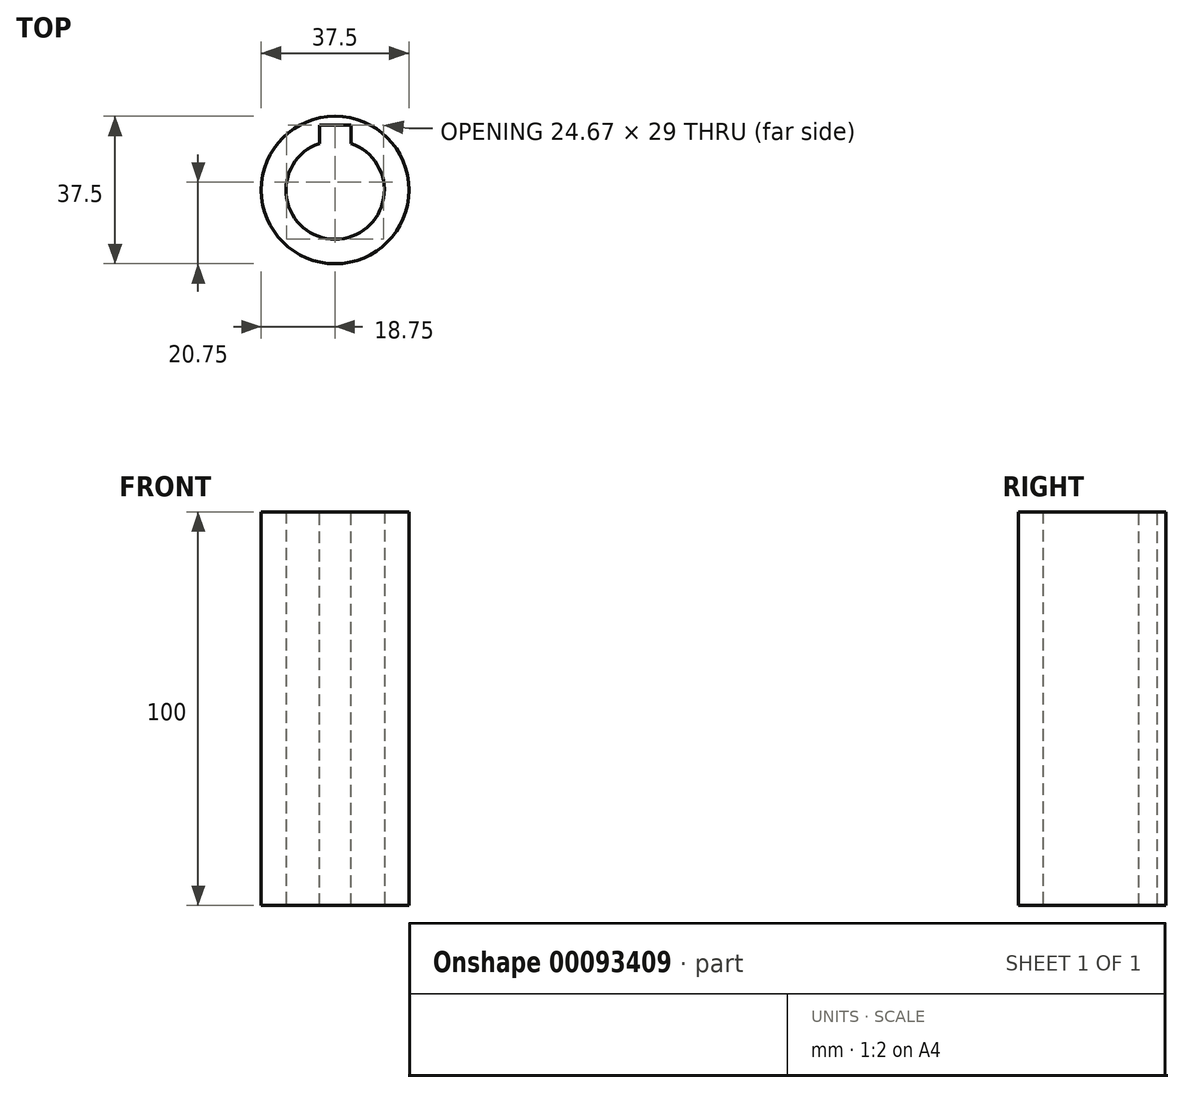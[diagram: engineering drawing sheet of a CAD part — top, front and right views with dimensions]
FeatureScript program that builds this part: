
annotation { "Feature Type Name" : "Feature", "Feature Type Description" : "" }
export const myFeature = defineFeature(function(context is Context, id is Id, definition is map)
    precondition{}
    {
        {
            var Q0;
            Q0=qCreatedBy(makeId("Top.planeOp"),FACE);
            var sketch = newSketch(context, id + "F0", { "sketchPlane" : qUnion([Q0])});
            skCircle(sketch, "E0", {"center": v(0, 0) * mm, "radius": 18.75 * mm});
            skCircle(sketch, "E1", {"center": v(0, 0) * mm, "radius": 12.5 * mm});
            skSolve(sketch);
        }
        {
            var Q0;
            Q0 = qSketchRegion(id + "F0", true);
            extrude(context, id + "F1", {"entities" : qUnion([Q0]), "depth" : 100 * mm, "offsetDistance" : 25.4 * mm});
        }
        {
            var Q0;
            Q0=makeQuery(id+"F1.opExtrude","CAP_FACE",FACE,{"disambiguationData":[OSD([sQuery(id+"F0.wireOp",EDGE,"E0"),sQuery(id+"F0.wireOp",EDGE,"E1")])],"isStart":false});
            var sketch = newSketch(context, id + "F2", { "sketchPlane" : qUnion([Q0])});
            skCircle(sketch, "E2", {"center": v(0, 0) * mm, "radius": 12.5 * mm});
            skLineSegment(sketch, "E3.bottom", {"start": v(4, 16.5) * mm, "end": v(-4, 16.5) * mm});
            skLineSegment(sketch, "E3.top", {"start": v(4, 8.5) * mm, "end": v(-4, 8.5) * mm});
            skLineSegment(sketch, "E3.left", {"start": v(4, 16.5) * mm, "end": v(4, 8.5) * mm});
            skLineSegment(sketch, "E3.right", {"start": v(-4, 16.5) * mm, "end": v(-4, 8.5) * mm});
            skPoint(sketch, "E3.middle", {"position": v(0, 12.5) * mm});
            skSolve(sketch);
        }
        {
            var Q0;
            Q0 = qSketchRegion(id + "F2", true);
            extrude(context, id + "F3", {"entities" : qUnion([Q0]), "operationType" : NewBodyOperationType.REMOVE, "endBound" : BoundingType.THROUGH_ALL, "oppositeDirection" : true, "depth" : 25.4 * mm, "offsetDistance" : 25.4 * mm});
        }
    });
